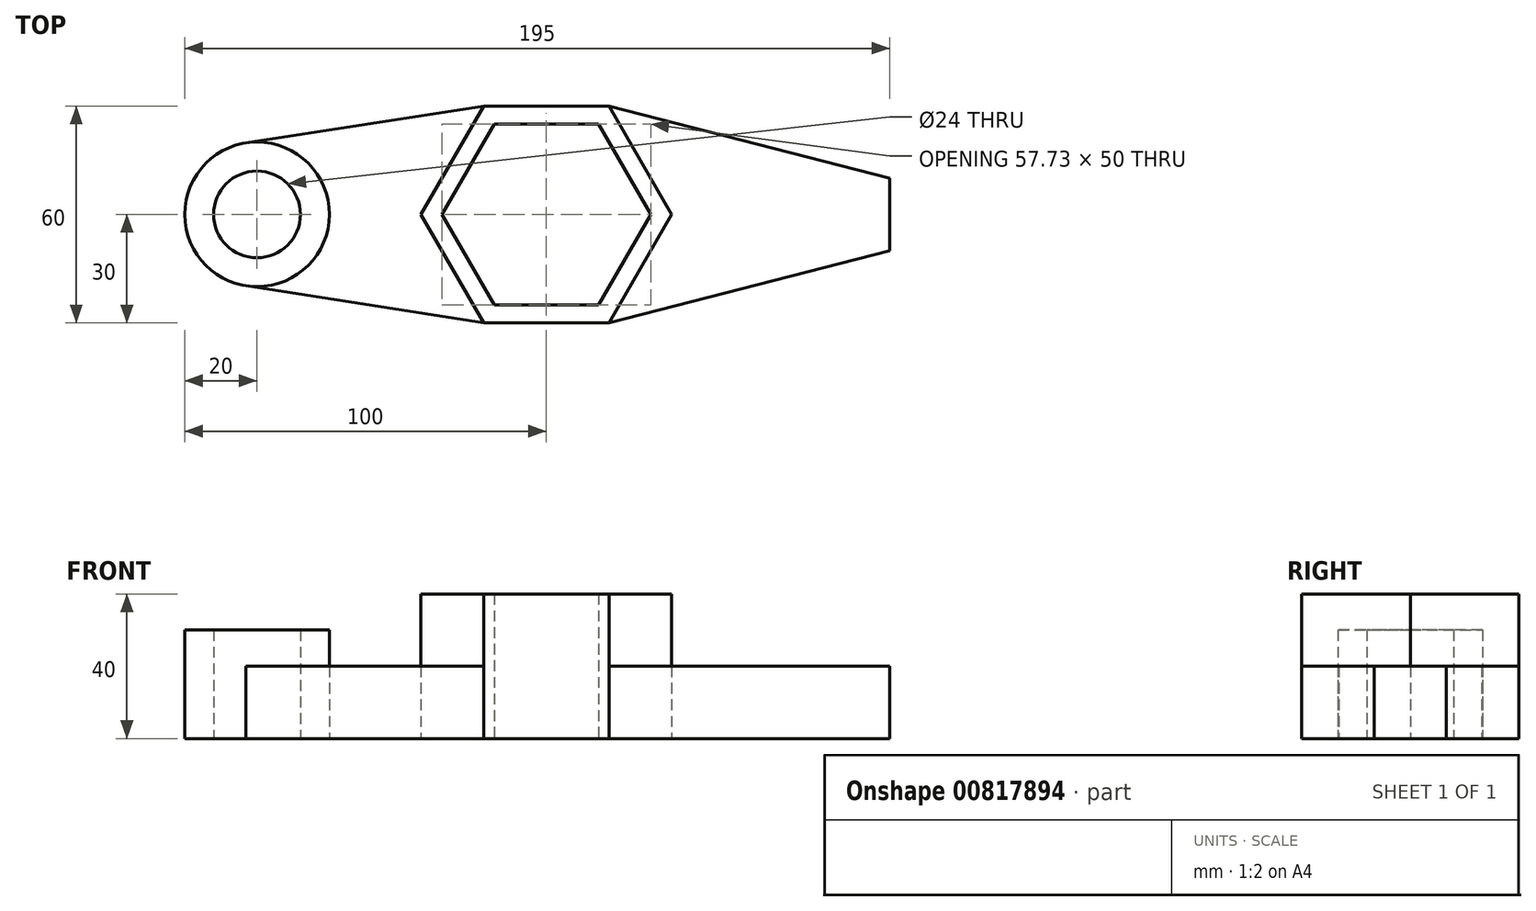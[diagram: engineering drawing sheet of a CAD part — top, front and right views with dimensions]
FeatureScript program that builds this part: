
annotation { "Feature Type Name" : "Feature", "Feature Type Description" : "" }
export const myFeature = defineFeature(function(context is Context, id is Id, definition is map)
    precondition{}
    {
        {
            var Q0;
            Q0=qCreatedBy(makeId("Top.planeOp"),FACE);
            var sketch = newSketch(context, id + "F0", { "sketchPlane" : qUnion([Q0])});
            skLineSegment(sketch, "E0.0", {"start": v(-14.43, 25) * mm, "end": v(14.43, 25) * mm});
            skLineSegment(sketch, "E0.1", {"start": v(14.43, 25) * mm, "end": v(28.87, 0) * mm});
            skLineSegment(sketch, "E0.2", {"start": v(28.87, 0) * mm, "end": v(14.43, -25) * mm});
            skLineSegment(sketch, "E0.3", {"start": v(14.43, -25) * mm, "end": v(-14.43, -25) * mm});
            skLineSegment(sketch, "E0.4", {"start": v(-14.43, -25) * mm, "end": v(-28.87, 0) * mm});
            skLineSegment(sketch, "E0.5", {"start": v(-28.87, 0) * mm, "end": v(-14.43, 25) * mm});
            skPoint(sketch, "E0.0.midPoint", {"position": v(0, 25) * mm});
            skLineSegment(sketch, "E1.0", {"start": v(-17.32, 30) * mm, "end": v(17.32, 30) * mm});
            skLineSegment(sketch, "E1.1", {"start": v(17.32, 30) * mm, "end": v(34.64, 0) * mm});
            skLineSegment(sketch, "E1.2", {"start": v(34.64, 0) * mm, "end": v(17.32, -30) * mm});
            skLineSegment(sketch, "E1.3", {"start": v(17.32, -30) * mm, "end": v(-17.32, -30) * mm});
            skLineSegment(sketch, "E1.4", {"start": v(-17.32, -30) * mm, "end": v(-34.64, 0) * mm});
            skLineSegment(sketch, "E1.5", {"start": v(-34.64, 0) * mm, "end": v(-17.32, 30) * mm});
            skPoint(sketch, "E1.0.midPoint", {"position": v(0, 30) * mm});
            skPoint(sketch, "E0.cCircle.center.orphan", {"position": v(0, 0) * mm});
            skLineSegment(sketch, "E2", {"start": v(0, -30) * mm, "end": v(80, -30) * mm});
            skLineSegment(sketch, "E3", {"start": v(0, -30) * mm, "end": v(-80, -30) * mm});
            skCircle(sketch, "E4", {"center": v(-80, 0) * mm, "radius": 20 * mm});
            skCircle(sketch, "E5", {"center": v(-80, 0) * mm, "radius": 12 * mm});
            skLineSegment(sketch, "E6", {"start": v(-17.32, 30) * mm, "end": v(-83.08, 19.76) * mm});
            skLineSegment(sketch, "E7", {"start": v(-17.32, -30) * mm, "end": v(-83.08, -19.76) * mm});
            skLineSegment(sketch, "E8", {"start": v(80, 0) * mm, "end": v(95, 0) * mm});
            skLineSegment(sketch, "E9", {"start": v(95, 0) * mm, "end": v(95, 10) * mm});
            skLineSegment(sketch, "E10", {"start": v(95, 10) * mm, "end": v(95, -10) * mm});
            skLineSegment(sketch, "E11", {"start": v(17.32, 30) * mm, "end": v(95, 10) * mm});
            skLineSegment(sketch, "E12", {"start": v(95, -10) * mm, "end": v(17.32, -30) * mm});
            skLineSegment(sketch, "E13", {"start": v(80, -30) * mm, "end": v(80, 36.84) * mm});
            skLineSegment(sketch, "E14", {"start": v(80, 36.84) * mm, "end": v(83, 36.84) * mm});
            skLineSegment(sketch, "E15", {"start": v(83, 36.84) * mm, "end": v(83, -30) * mm});
            skLineSegment(sketch, "E16", {"start": v(83, -30) * mm, "end": v(80, -30) * mm});
            skLineSegment(sketch, "E17", {"start": v(80, 36.84) * mm, "end": v(77, 36.84) * mm});
            skLineSegment(sketch, "E18", {"start": v(77, 36.84) * mm, "end": v(77, -30) * mm});
            skSolve(sketch);
        }
        {
            var Q0;
            Q0=makeQuery(id+"F0.imprint","IMPRINT",FACE,{"disambiguationData":[TD([[makeQuery(id+"F0.imprint","IMPRINT",EDGE,{"derivedFrom":sQuery(id+"F0.wireOp",EDGE,"E0.0")}),1.0]])]});
            extrude(context, id + "F1", {"entities" : qUnion([Q0]), "depth" : 40 * mm, "offsetDistance" : 25 * mm});
        }
        {
            var Q0;
            Q0=makeQuery(id+"F0.imprint","IMPRINT",FACE,{"disambiguationData":[TD([[makeQuery(id+"F0.imprint","IMPRINT",EDGE,{"derivedFrom":sQuery(id+"F0.wireOp",EDGE,"E5")}),-1.0]])]});
            extrude(context, id + "F2", {"entities" : qUnion([Q0]), "depth" : 30 * mm, "offsetDistance" : 25 * mm});
        }
        {
            var Q0;
            Q0=makeQuery(id+"F0.imprint","IMPRINT",FACE,{"disambiguationData":[TD([[makeQuery(id+"F0.imprint","IMPRINT",EDGE,{"derivedFrom":sQuery(id+"F0.wireOp",EDGE,"E1.4")}),1.0]])]});
            var Q1;
            {var subQ5=sQuery(id+"F0.wireOp",EDGE,"E1.1");Q1=makeQuery(id+"F0.imprint","IMPRINT",FACE,{"disambiguationData":[TD([[makeQuery(id+"F0.imprint","IMPRINT",EDGE,{"derivedFrom":subQ5}),1.0]])]});}
            var Q2;
            {var subQ0=sQuery(id+"F0.wireOp",EDGE,"E10");var subQ1=sQuery(id+"F0.wireOp",EDGE,"E8");var subQ2=makeQuery(id+"F0.imprint","INTERSECT",VERTEX,{"derivedFrom":[subQ1,subQ0]});Q2=makeQuery(id+"F0.imprint","IMPRINT",FACE,{"disambiguationData":[TD([[makeQuery(id+"F0.imprint","IMPRINT",EDGE,{"disambiguationData":[TD([[subQ2,1.0]])],"derivedFrom":subQ1}),-1.0]])]});}
            var Q3;
            {var subQ0=sQuery(id+"F0.wireOp",EDGE,"E10");var subQ1=sQuery(id+"F0.wireOp",EDGE,"E8");var subQ2=makeQuery(id+"F0.imprint","INTERSECT",VERTEX,{"derivedFrom":[subQ1,subQ0]});Q3=makeQuery(id+"F0.imprint","IMPRINT",FACE,{"disambiguationData":[TD([[makeQuery(id+"F0.imprint","IMPRINT",EDGE,{"disambiguationData":[TD([[subQ2,1.0]])],"derivedFrom":subQ1}),1.0]])]});}
            var Q4;
            {var subQ0=sQuery(id+"F0.wireOp",EDGE,"E13");var subQ1=sQuery(id+"F0.wireOp",EDGE,"E8");var subQ2=makeQuery(id+"F0.imprint","INTERSECT",VERTEX,{"derivedFrom":[subQ1,subQ0]});Q4=makeQuery(id+"F0.imprint","IMPRINT",FACE,{"disambiguationData":[TD([[makeQuery(id+"F0.imprint","IMPRINT",EDGE,{"disambiguationData":[TD([[subQ2,-1.0]])],"derivedFrom":subQ1}),-1.0]])]});}
            var Q5;
            {var subQ2=sQuery(id+"F0.wireOp",EDGE,"E11");var subQ6=sQuery(id+"F0.wireOp",EDGE,"E18");var subQ7=makeQuery(id+"F0.imprint","INTERSECT",VERTEX,{"derivedFrom":[subQ2,subQ6]});Q5=makeQuery(id+"F0.imprint","IMPRINT",FACE,{"disambiguationData":[TD([[makeQuery(id+"F0.imprint","IMPRINT",EDGE,{"disambiguationData":[TD([[subQ7,-1.0]])],"derivedFrom":subQ2}),-1.0]])]});}
            var Q6;
            {var subQ0=sQuery(id+"F0.wireOp",EDGE,"E13");var subQ1=sQuery(id+"F0.wireOp",EDGE,"E8");var subQ2=makeQuery(id+"F0.imprint","INTERSECT",VERTEX,{"derivedFrom":[subQ1,subQ0]});Q6=makeQuery(id+"F0.imprint","IMPRINT",FACE,{"disambiguationData":[TD([[makeQuery(id+"F0.imprint","IMPRINT",EDGE,{"disambiguationData":[TD([[subQ2,-1.0]])],"derivedFrom":subQ1}),1.0]])]});}
            extrude(context, id + "F3", {"entities" : qUnion([Q0, Q1, Q2, Q3, Q4, Q5, Q6]), "depth" : 20 * mm, "offsetDistance" : 25 * mm});
        }
        {
            var Q0;
            Q0=makeQuery(id+"F3.opExtrude","SWEPT_FACE",FACE,{"disambiguationData":[OSD([sQuery(id+"F0.wireOp",EDGE,"E12")])]});
            var sketch = newSketch(context, id + "F4", { "sketchPlane" : qUnion([Q0])});
            skLineSegment(sketch, "E19.0.0", {"start": v(9.3, 0) * mm, "end": v(89.5, 0) * mm});
            skLineSegment(sketch, "E19.0.1", {"start": v(89.5, 0) * mm, "end": v(89.5, 20) * mm});
            skLineSegment(sketch, "E19.0.2", {"start": v(89.5, 20) * mm, "end": v(9.3, 20) * mm});
            skLineSegment(sketch, "E19.0.3", {"start": v(9.3, 20) * mm, "end": v(9.3, 0) * mm});
            skLineSegment(sketch, "E20", {"start": v(89.5, 0) * mm, "end": v(89.5, 15) * mm});
            skLineSegment(sketch, "E21", {"start": v(89.5, 15) * mm, "end": v(74.5, 15) * mm});
            skCircle(sketch, "E22", {"center": v(74.5, 15) * mm, "radius": 6 * mm});
            skCircle(sketch, "E23", {"center": v(74.5, 20) * mm, "radius": 15 * mm});
            skSolve(sketch);
        }
    });
